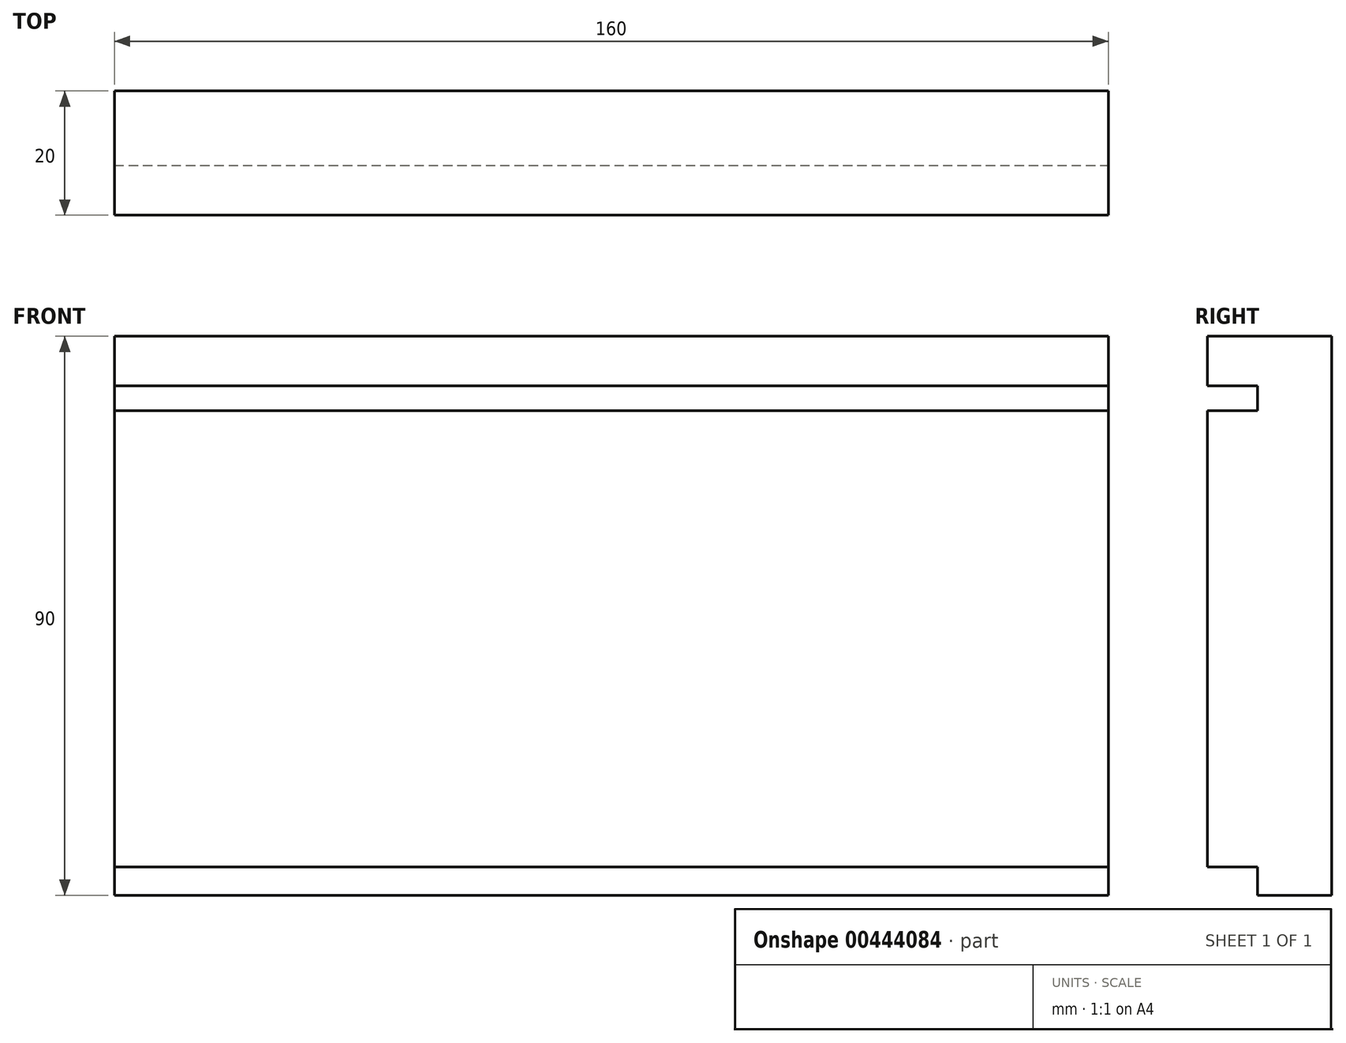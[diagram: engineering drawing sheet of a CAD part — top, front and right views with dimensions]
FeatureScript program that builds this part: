
annotation { "Feature Type Name" : "Feature", "Feature Type Description" : "" }
export const myFeature = defineFeature(function(context is Context, id is Id, definition is map)
    precondition{}
    {
        {
            var Q0;
            Q0=qCreatedBy(makeId("Front.planeOp"),FACE);
            var sketch = newSketch(context, id + "F0", { "sketchPlane" : qUnion([Q0])});
            skLineSegment(sketch, "E0.bottom", {"start": v(-68.36, 51.78) * mm, "end": v(91.64, 51.78) * mm});
            skLineSegment(sketch, "E0.top", {"start": v(-68.36, -33.7) * mm, "end": v(91.64, -33.7) * mm});
            skLineSegment(sketch, "E0.left", {"start": v(-68.36, 51.78) * mm, "end": v(-68.36, -33.7) * mm});
            skLineSegment(sketch, "E0.right", {"start": v(91.64, 51.78) * mm, "end": v(91.64, -33.7) * mm});
            skLineSegment(sketch, "E1.top", {"start": v(-68.36, -38.22) * mm, "end": v(91.64, -38.22) * mm});
            skLineSegment(sketch, "E1.left", {"start": v(-68.36, -33.7) * mm, "end": v(-68.36, -38.22) * mm});
            skLineSegment(sketch, "E1.right", {"start": v(91.64, -33.7) * mm, "end": v(91.64, -38.22) * mm});
            skSolve(sketch);
        }
        {
            var Q0;
            Q0=makeQuery(id+"F0.imprint","IMPRINT",FACE,{"disambiguationData":[TD([[makeQuery(id+"F0.imprint","IMPRINT",EDGE,{"derivedFrom":sQuery(id+"F0.wireOp",EDGE,"E0.bottom")}),-1.0]])]});
            extrude(context, id + "F1", {"entities" : qUnion([Q0]), "depth" : 20 * mm});
        }
        {
            var Q0;
            Q0=makeQuery(id+"F0.imprint","IMPRINT",FACE,{"disambiguationData":[TD([[makeQuery(id+"F0.imprint","IMPRINT",EDGE,{"derivedFrom":sQuery(id+"F0.wireOp",EDGE,"E1.top")}),1.0]])]});
            extrude(context, id + "F2", {"entities" : qUnion([Q0]), "operationType" : NewBodyOperationType.ADD, "depth" : 12 * mm});
        }
        {
            var Q0;
            Q0=makeQuery(id+"F1.opExtrude","CAP_FACE",FACE,{"disambiguationData":[OSD([sQuery(id+"F0.wireOp",EDGE,"E0.bottom"),sQuery(id+"F0.wireOp",EDGE,"E0.top"),sQuery(id+"F0.wireOp",EDGE,"E0.left"),sQuery(id+"F0.wireOp",EDGE,"E0.right")])],"isStart":false});
            var sketch = newSketch(context, id + "F3", { "sketchPlane" : qUnion([Q0])});
            skLineSegment(sketch, "E2.bottom", {"start": v(-68.36, 43.78) * mm, "end": v(91.64, 43.78) * mm});
            skLineSegment(sketch, "E2.top", {"start": v(-68.36, 39.78) * mm, "end": v(91.64, 39.78) * mm});
            skLineSegment(sketch, "E2.left", {"start": v(-68.36, 43.78) * mm, "end": v(-68.36, 39.78) * mm});
            skLineSegment(sketch, "E2.right", {"start": v(91.64, 43.78) * mm, "end": v(91.64, 39.78) * mm});
            skSolve(sketch);
        }
        {
            var Q0;
            Q0=makeQuery(id+"F3.imprint","IMPRINT",FACE,{"disambiguationData":[TD([[makeQuery(id+"F3.imprint","IMPRINT",EDGE,{"derivedFrom":sQuery(id+"F3.wireOp",EDGE,"E2.bottom")}),-1.0]])]});
            extrude(context, id + "F4", {"entities" : qUnion([Q0]), "operationType" : NewBodyOperationType.REMOVE, "oppositeDirection" : true, "depth" : 8 * mm});
        }
    });
